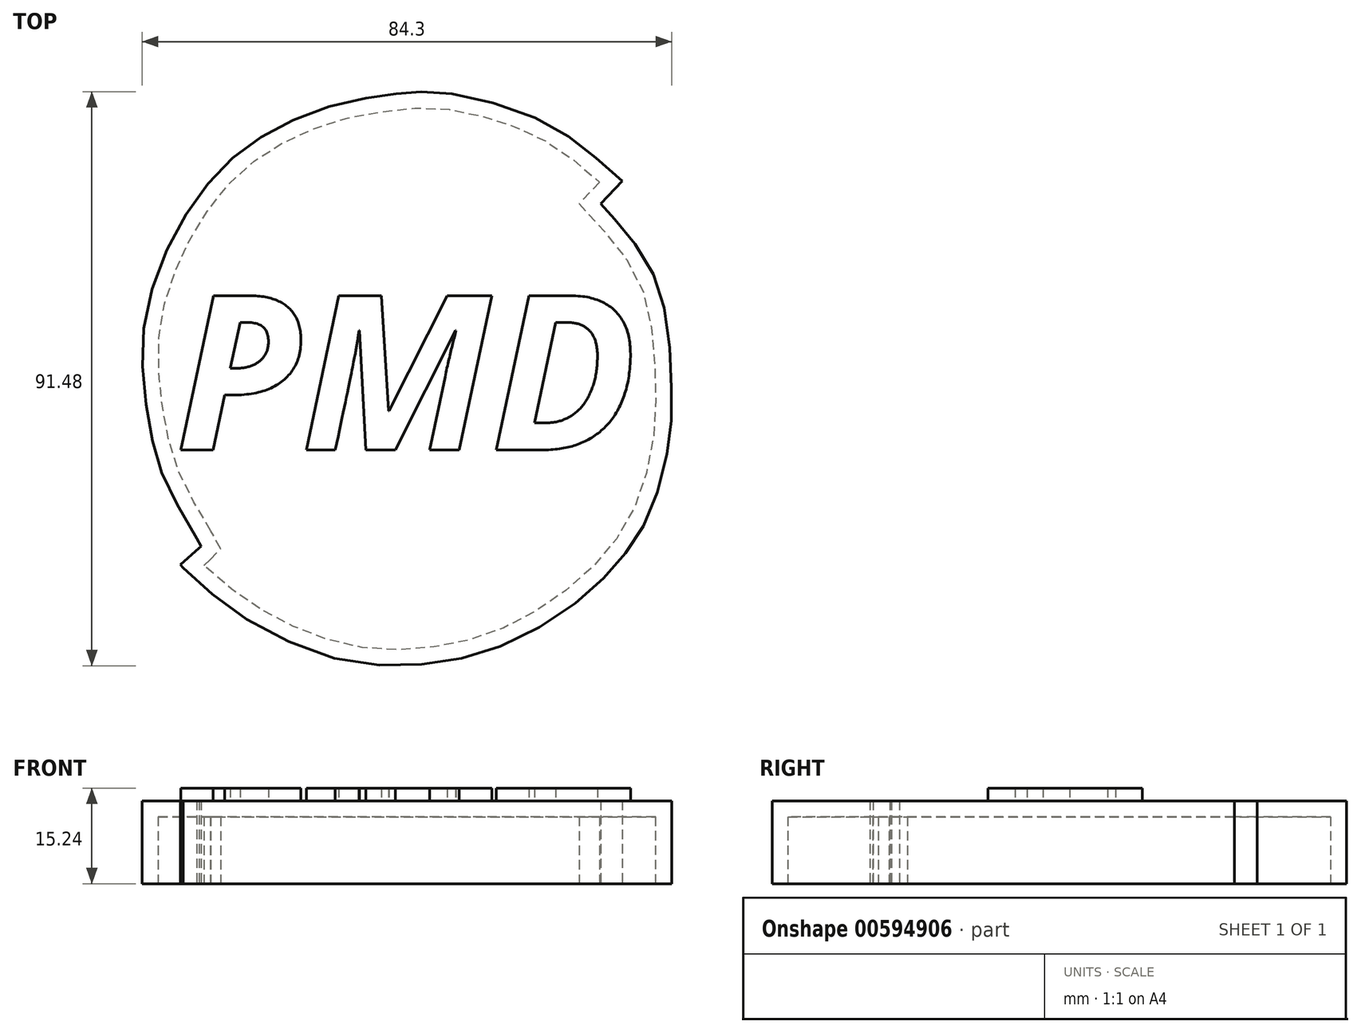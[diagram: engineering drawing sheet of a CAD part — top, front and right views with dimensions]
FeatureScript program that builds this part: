
annotation { "Feature Type Name" : "Feature", "Feature Type Description" : "" }
export const myFeature = defineFeature(function(context is Context, id is Id, definition is map)
    precondition{}
    {
        {
            var Q0;
            Q0=qCreatedBy(makeId("Top.planeOp"),FACE);
            var sketch = newSketch(context, id + "F0", { "sketchPlane" : qUnion([Q0])});
            skFitSpline(sketch, "E0", {"points": [v(-108.62, -27.45) * mm, v(-113.42, -18.81) * mm, v(-115.72, -11.8) * mm, v(-117.16, -2.3) * mm, v(-116.9, 7.39) * mm, v(-113.46, 18.4) * mm, v(-108.2, 27.37) * mm, v(-102.28, 33.75) * mm, v(-95.09, 38.4) * mm, v(-85.95, 41.86) * mm, v(-78, 43.3) * mm, v(-73.7, 43.72) * mm, v(-67.4, 43.34) * mm, v(-55.12, 39.74) * mm, v(-47.1, 34.87) * mm, v(-40.92, 29.5) * mm], "startDerivative": vector(-75.75, 126.35) * mm, "endDerivative": vector(94.18, -86.15) * mm});
            skLineSegment(sketch, "E1", {"start": v(-40.92, 29.5) * mm, "end": v(-44.3, 25.87) * mm});
            skFitSpline(sketch, "E2", {"points": [v(-44.3, 25.87) * mm, v(-42.17, 23.54) * mm, v(-37.12, 16.91) * mm, v(-33.92, 7.84) * mm, v(-33.05, -4.28) * mm, v(-33.49, -12.29) * mm, v(-36.4, -23.05) * mm, v(-40.7, -30.23) * mm, v(-47.22, -36.86) * mm, v(-59.17, -44.2) * mm, v(-71.2, -47.34) * mm, v(-85.17, -46.9) * mm, v(-101.04, -40.12) * mm, v(-110.82, -32.13) * mm], "startDerivative": vector(44.29, -47.57) * mm, "endDerivative": vector(-104.55, 97.2) * mm});
            skLineSegment(sketch, "E3", {"start": v(-110.82, -32.13) * mm, "end": v(-111.25, -31.64) * mm});
            skLineSegment(sketch, "E4", {"start": v(-111.25, -31.64) * mm, "end": v(-108.25, -29) * mm});
            skLineSegment(sketch, "E5", {"start": v(-108.25, -29) * mm, "end": v(-107.97, -28.7) * mm});
            skLineSegment(sketch, "E6", {"start": v(-107.97, -28.7) * mm, "end": v(-108.62, -27.45) * mm});
            skSolve(sketch);
        }
        {
            var Q0;
            Q0 = qSketchRegion(id + "F0", true);
            extrude(context, id + "F1", {"entities" : qUnion([Q0]), "depth" : 13.2 * mm, "offsetDistance" : 25.4 * mm});
        }
        {
            var Q0;
            Q0=makeQuery(id+"F1.opExtrude","CAP_FACE",FACE,{"disambiguationData":[OSD([sQuery(id+"F0.wireOp",EDGE,"E0"),sQuery(id+"F0.wireOp",EDGE,"E1"),sQuery(id+"F0.wireOp",EDGE,"E2"),sQuery(id+"F0.wireOp",EDGE,"E3"),sQuery(id+"F0.wireOp",EDGE,"E4"),sQuery(id+"F0.wireOp",EDGE,"E5"),sQuery(id+"F0.wireOp",EDGE,"E6")])],"isStart":true});
            shell(context, id + "F2", {"entities" : qUnion([Q0]), "thickness" : 2.54 * mm});
        }
        {
            var Q0;
            Q0=makeQuery(id+"F1.opExtrude","CAP_FACE",FACE,{"disambiguationData":[OSD([sQuery(id+"F0.wireOp",EDGE,"E0"),sQuery(id+"F0.wireOp",EDGE,"E1"),sQuery(id+"F0.wireOp",EDGE,"E2"),sQuery(id+"F0.wireOp",EDGE,"E3"),sQuery(id+"F0.wireOp",EDGE,"E4"),sQuery(id+"F0.wireOp",EDGE,"E5"),sQuery(id+"F0.wireOp",EDGE,"E6")])],"isStart":false});
            var sketch = newSketch(context, id + "F3", { "sketchPlane" : qUnion([Q0])});
            skText(sketch, "E7", { "text": "PMD", "fontName": "OpenSans-BoldItalic.ttf"});
            const initialGuessF3  = {"E7": [-0.11207, -0.01333, 1, 0, 0.02478]};
            skSetInitialGuess(sketch, initialGuessF3);
            skSolve(sketch);
        }
        {
            var Q0;
            Q0 = qSketchRegion(id + "F3", true);
            extrude(context, id + "F4", {"entities" : qUnion([Q0]), "operationType" : NewBodyOperationType.ADD, "depth" : 2.03 * mm, "offsetDistance" : 25.4 * mm});
        }
    });
